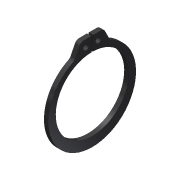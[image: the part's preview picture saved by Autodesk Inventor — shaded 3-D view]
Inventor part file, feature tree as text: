
AUTODESK INVENTOR PART (.ipt)
format: ipt  version: 2013 (Build 170138000, 138)  size: 96,256 bytes
history: native  units: in
note: dims shown in document units (in); Inventor stores cm internally (conversion verified against a paired STEP export)
features: fillet x1, other x1, imported_body x1
ambient origin geometry x8: Origin, YZ Plane, XZ Plane, XY Plane, X Axis, Y Axis, Z Axis, Center Point
feature tree (3):
  fillet  "Fillet1"  [1 undecoded]
  other  "217-2428-028 Rev1_97633A2501"
  imported_body  "Base1"
note: 1 required parameter value undecoded (feature->parameter linkage not recoverable at this tier; creation-order binding heuristic only, values carry confidence <= 0.55)
